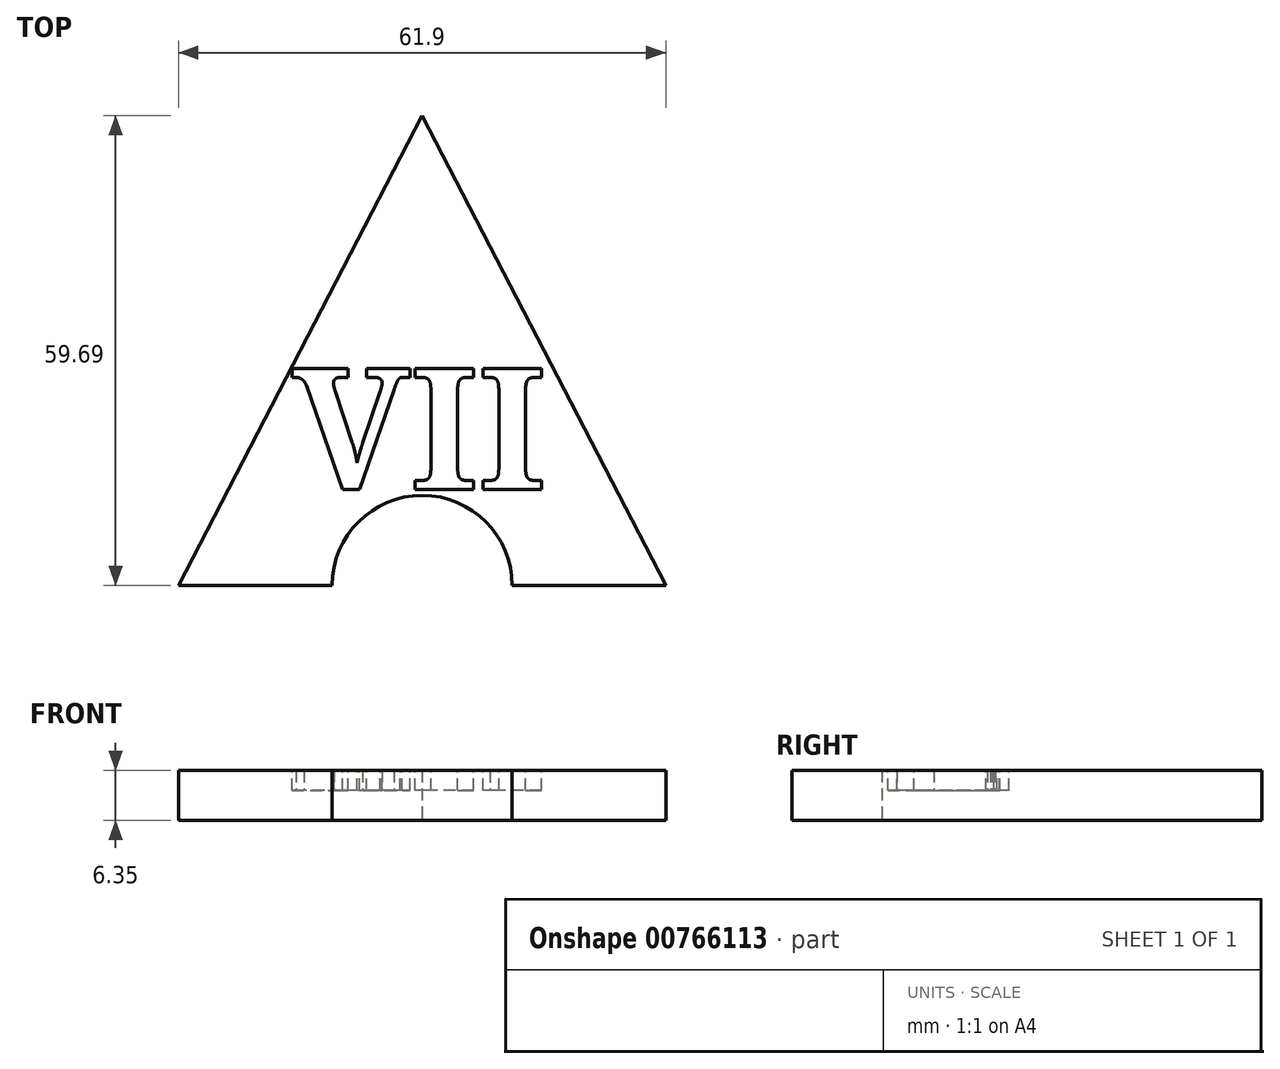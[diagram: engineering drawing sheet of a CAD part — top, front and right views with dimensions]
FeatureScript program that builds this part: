
annotation { "Feature Type Name" : "Feature", "Feature Type Description" : "" }
export const myFeature = defineFeature(function(context is Context, id is Id, definition is map)
    precondition{}
    {
        {
            var Q0;
            Q0=qCreatedBy(makeId("Top.planeOp"),FACE);
            var sketch = newSketch(context, id + "F0", { "sketchPlane" : qUnion([Q0])});
            skCircle(sketch, "E0.cCircle", {"center": v(0, -2.1) * mm, "radius": 17.87 * mm, "construction": true});
            skLineSegment(sketch, "E0.0", {"start": v(30.95, -19.97) * mm, "end": v(-30.95, -19.97) * mm});
            skLineSegment(sketch, "E0.1", {"start": v(-30.95, -19.97) * mm, "end": v(0, 39.72) * mm});
            skLineSegment(sketch, "E0.2", {"start": v(0, 39.72) * mm, "end": v(30.95, -19.97) * mm});
            skPoint(sketch, "E0.0.midPoint", {"position": v(0, -19.97) * mm});
            skSolve(sketch);
        }
        {
            var Q0;
            Q0 = qSketchRegion(id + "F0", true);
            extrude(context, id + "F1", {"entities" : qUnion([Q0]), "depth" : 6.35 * mm, "offsetDistance" : 25.4 * mm});
        }
        {
            var Q0;
            Q0=sQuery(id+"F0.wireOp",VERTEX,"E0.0.midPoint");
            var Q1;
            Q1=makeQuery(id+"F1.opExtrude","SWEPT_BODY",BODY,{"disambiguationData":[OSD([sQuery(id+"F0.wireOp",EDGE,"E0.0"),sQuery(id+"F0.wireOp",EDGE,"E0.1"),sQuery(id+"F0.wireOp",EDGE,"E0.2")])]});
            hole(context, id + "F2", {"style" : HoleStyle.SIMPLE, "endStyle" : HoleEndStyle.THROUGH, "oppositeDirection" : true, "holeDiameter" : 22.86 * mm, "majorDiameter" : 6.35 * mm, "isTappedThrough" : true, "tappedDepth" : 12.7 * mm, "tapClearance" : 3, "locations" : qUnion([Q0]), "scope" : qUnion([Q1])});
        }
        {
            var Q0;
            Q0=makeQuery(id+"F1.opExtrude","CAP_FACE",FACE,{"disambiguationData":[OSD([sQuery(id+"F0.wireOp",EDGE,"E0.0"),sQuery(id+"F0.wireOp",EDGE,"E0.1"),sQuery(id+"F0.wireOp",EDGE,"E0.2")])],"isStart":false});
            var sketch = newSketch(context, id + "F3", { "sketchPlane" : qUnion([Q0])});
            skText(sketch, "E1", { "text": "VII", "fontName": "NotoSerif-Bold.ttf"});
            const initialGuessF3  = {"E1": [-0.01654, -0.00778, 1, 0, 0.0155]};
            skSetInitialGuess(sketch, initialGuessF3);
            skSolve(sketch);
        }
        {
            var Q0;
            Q0 = qSketchRegion(id + "F3", true);
            extrude(context, id + "F4", {"entities" : qUnion([Q0]), "operationType" : NewBodyOperationType.REMOVE, "oppositeDirection" : true, "depth" : 2.54 * mm, "offsetDistance" : 25.4 * mm});
        }
    });
